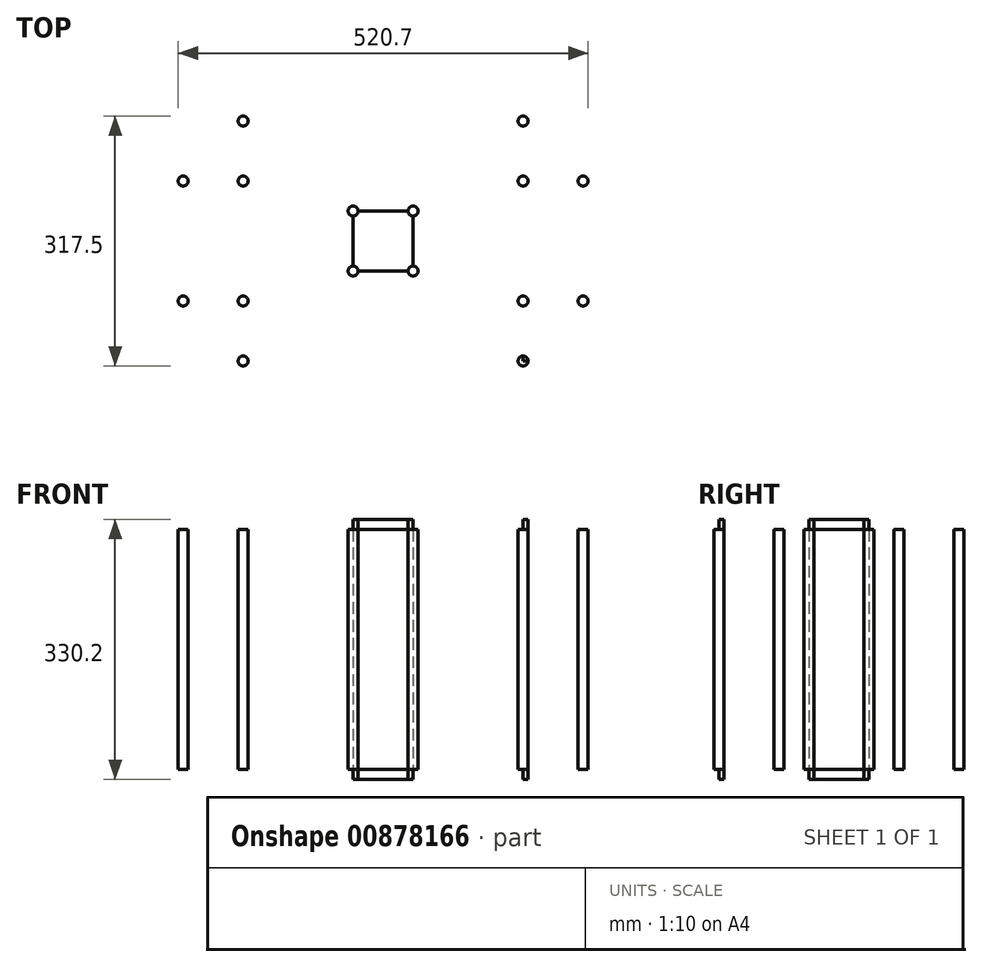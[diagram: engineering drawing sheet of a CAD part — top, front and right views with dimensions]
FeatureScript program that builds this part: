
annotation { "Feature Type Name" : "Feature", "Feature Type Description" : "" }
export const myFeature = defineFeature(function(context is Context, id is Id, definition is map)
    precondition{}
    {
        {
            var Q0;
            Q0=qCreatedBy(makeId("Top.planeOp"),FACE);
            var sketch = newSketch(context, id + "F0", { "sketchPlane" : qUnion([Q0])});
            skLineSegment(sketch, "E0.bottom", {"start": v(254, -152.4) * mm, "end": v(-254, -152.4) * mm});
            skLineSegment(sketch, "E0.top", {"start": v(254, 152.4) * mm, "end": v(-254, 152.4) * mm});
            skLineSegment(sketch, "E0.left", {"start": v(254, -152.4) * mm, "end": v(254, 152.4) * mm});
            skLineSegment(sketch, "E0.right", {"start": v(-254, -152.4) * mm, "end": v(-254, 152.4) * mm});
            skPoint(sketch, "E0.middle", {"position": v(0, 0) * mm});
            skLineSegment(sketch, "E1.bottom", {"start": v(-254, 152.4) * mm, "end": v(-177.8, 152.4) * mm});
            skLineSegment(sketch, "E1.top", {"start": v(-254, 76.2) * mm, "end": v(-177.8, 76.2) * mm});
            skLineSegment(sketch, "E1.left", {"start": v(-254, 152.4) * mm, "end": v(-254, 76.2) * mm});
            skLineSegment(sketch, "E1.right", {"start": v(-177.8, 152.4) * mm, "end": v(-177.8, 76.2) * mm});
            skLineSegment(sketch, "E2.bottom", {"start": v(254, 152.4) * mm, "end": v(177.8, 152.4) * mm});
            skLineSegment(sketch, "E2.top", {"start": v(254, 76.2) * mm, "end": v(177.8, 76.2) * mm});
            skLineSegment(sketch, "E2.left", {"start": v(254, 152.4) * mm, "end": v(254, 76.2) * mm});
            skLineSegment(sketch, "E2.right", {"start": v(177.8, 152.4) * mm, "end": v(177.8, 76.2) * mm});
            skLineSegment(sketch, "E3.bottom", {"start": v(254, -152.4) * mm, "end": v(177.8, -152.4) * mm});
            skLineSegment(sketch, "E3.top", {"start": v(254, -76.2) * mm, "end": v(177.8, -76.2) * mm});
            skLineSegment(sketch, "E3.left", {"start": v(254, -152.4) * mm, "end": v(254, -76.2) * mm});
            skLineSegment(sketch, "E3.right", {"start": v(177.8, -152.4) * mm, "end": v(177.8, -76.2) * mm});
            skLineSegment(sketch, "E4.bottom", {"start": v(-254, -152.4) * mm, "end": v(-177.8, -152.4) * mm});
            skLineSegment(sketch, "E4.top", {"start": v(-254, -76.2) * mm, "end": v(-177.8, -76.2) * mm});
            skLineSegment(sketch, "E4.left", {"start": v(-254, -152.4) * mm, "end": v(-254, -76.2) * mm});
            skLineSegment(sketch, "E4.right", {"start": v(-177.8, -152.4) * mm, "end": v(-177.8, -76.2) * mm});
            skLineSegment(sketch, "E5.bottom", {"start": v(38.1, 38.1) * mm, "end": v(-38.1, 38.1) * mm});
            skLineSegment(sketch, "E5.top", {"start": v(38.1, -38.1) * mm, "end": v(-38.1, -38.1) * mm});
            skLineSegment(sketch, "E5.left", {"start": v(38.1, 38.1) * mm, "end": v(38.1, -38.1) * mm});
            skLineSegment(sketch, "E5.right", {"start": v(-38.1, 38.1) * mm, "end": v(-38.1, -38.1) * mm});
            skCircle(sketch, "E6", {"center": v(-177.8, 76.2) * mm, "radius": 6.35 * mm});
            skCircle(sketch, "E7", {"center": v(-254, 152.4) * mm, "radius": 6.35 * mm});
            skCircle(sketch, "E8", {"center": v(-177.8, 152.4) * mm, "radius": 6.35 * mm});
            skCircle(sketch, "E9", {"center": v(-254, 76.2) * mm, "radius": 6.35 * mm});
            skCircle(sketch, "E10", {"center": v(-254, -152.4) * mm, "radius": 6.35 * mm});
            skCircle(sketch, "E11", {"center": v(-254, -76.2) * mm, "radius": 6.35 * mm});
            skCircle(sketch, "E12", {"center": v(-177.8, -152.4) * mm, "radius": 6.35 * mm});
            skCircle(sketch, "E13", {"center": v(-177.8, -76.2) * mm, "radius": 6.35 * mm});
            skCircle(sketch, "E14", {"center": v(-38.1, 38.1) * mm, "radius": 6.35 * mm});
            skCircle(sketch, "E15", {"center": v(-38.1, -38.1) * mm, "radius": 6.35 * mm});
            skCircle(sketch, "E16", {"center": v(38.1, -38.1) * mm, "radius": 6.35 * mm});
            skCircle(sketch, "E17", {"center": v(38.1, 38.1) * mm, "radius": 6.35 * mm});
            skCircle(sketch, "E18", {"center": v(177.8, -152.4) * mm, "radius": 6.35 * mm});
            skCircle(sketch, "E19", {"center": v(177.8, -76.2) * mm, "radius": 6.35 * mm});
            skCircle(sketch, "E20", {"center": v(254, -152.4) * mm, "radius": 6.35 * mm});
            skCircle(sketch, "E21", {"center": v(254, -76.2) * mm, "radius": 6.35 * mm});
            skCircle(sketch, "E22", {"center": v(177.8, 76.2) * mm, "radius": 6.35 * mm});
            skCircle(sketch, "E23", {"center": v(177.8, 152.4) * mm, "radius": 6.35 * mm});
            skCircle(sketch, "E24", {"center": v(254, 152.4) * mm, "radius": 6.35 * mm});
            skCircle(sketch, "E25", {"center": v(254, 76.2) * mm, "radius": 6.35 * mm});
            skSolve(sketch);
        }
        {
            var Q0;
            {var subQ11=sQuery(id+"F0.wireOp",EDGE,"E0.bottom");var subQ51=sQuery(id+"F0.wireOp",EDGE,"E18");var subQ52=makeQuery(id+"F0.imprint","INTERSECT",VERTEX,{"derivedFrom":[subQ11,subQ51]});Q0=makeQuery(id+"F0.imprint","IMPRINT",FACE,{"disambiguationData":[TD([[makeQuery(id+"F0.imprint","IMPRINT",EDGE,{"disambiguationData":[TD([[subQ52,-1.0]])],"derivedFrom":subQ11}),-1.0]])]});}
            var Q1;
            {var subQ5=sQuery(id+"F0.wireOp",EDGE,"E17");var subQ13=sQuery(id+"F0.wireOp",EDGE,"E5.bottom");var subQ14=makeQuery(id+"F0.imprint","INTERSECT",VERTEX,{"derivedFrom":[subQ13,subQ5]});Q1=makeQuery(id+"F0.imprint","IMPRINT",FACE,{"disambiguationData":[TD([[makeQuery(id+"F0.imprint","IMPRINT",EDGE,{"disambiguationData":[TD([[subQ14,-1.0]])],"derivedFrom":subQ13}),1.0]])]});}
            var Q2;
            {var subQ5=sQuery(id+"F0.wireOp",EDGE,"E24");var subQ13=sQuery(id+"F0.wireOp",EDGE,"E2.bottom");var subQ14=makeQuery(id+"F0.imprint","INTERSECT",VERTEX,{"derivedFrom":[subQ13,subQ5]});Q2=makeQuery(id+"F0.imprint","IMPRINT",FACE,{"disambiguationData":[TD([[makeQuery(id+"F0.imprint","IMPRINT",EDGE,{"disambiguationData":[TD([[subQ14,-1.0]])],"derivedFrom":subQ13}),1.0]])]});}
            var Q3;
            {var subQ5=sQuery(id+"F0.wireOp",EDGE,"E20");var subQ13=sQuery(id+"F0.wireOp",EDGE,"E3.bottom");var subQ14=makeQuery(id+"F0.imprint","INTERSECT",VERTEX,{"derivedFrom":[subQ13,subQ5]});Q3=makeQuery(id+"F0.imprint","IMPRINT",FACE,{"disambiguationData":[TD([[makeQuery(id+"F0.imprint","IMPRINT",EDGE,{"disambiguationData":[TD([[subQ14,-1.0]])],"derivedFrom":subQ13}),-1.0]])]});}
            var Q4;
            {var subQ5=sQuery(id+"F0.wireOp",EDGE,"E10");var subQ10=sQuery(id+"F0.wireOp",EDGE,"E4.bottom");var subQ15=makeQuery(id+"F0.imprint","INTERSECT",VERTEX,{"derivedFrom":[subQ10,subQ5]});Q4=makeQuery(id+"F0.imprint","IMPRINT",FACE,{"disambiguationData":[TD([[makeQuery(id+"F0.imprint","IMPRINT",EDGE,{"disambiguationData":[TD([[subQ15,-1.0]])],"derivedFrom":subQ10}),1.0]])]});}
            var Q5;
            {var subQ5=sQuery(id+"F0.wireOp",EDGE,"E1.bottom");var subQ7=sQuery(id+"F0.wireOp",EDGE,"E7");var subQ15=makeQuery(id+"F0.imprint","INTERSECT",VERTEX,{"derivedFrom":[subQ5,subQ7]});Q5=makeQuery(id+"F0.imprint","IMPRINT",FACE,{"disambiguationData":[TD([[makeQuery(id+"F0.imprint","IMPRINT",EDGE,{"disambiguationData":[TD([[subQ15,-1.0]])],"derivedFrom":subQ5}),-1.0]])]});}
            extrude(context, id + "F1", {"entities" : qUnion([Q0, Q1, Q2, Q3, Q4, Q5]), "depth" : 317.5 * mm, "offsetDistance" : 25.4 * mm});
        }
        {
            var Q0;
            {var subQ11=sQuery(id+"F0.wireOp",EDGE,"E0.bottom");var subQ51=sQuery(id+"F0.wireOp",EDGE,"E18");var subQ52=makeQuery(id+"F0.imprint","INTERSECT",VERTEX,{"derivedFrom":[subQ11,subQ51]});Q0=makeQuery(id+"F0.imprint","IMPRINT",FACE,{"disambiguationData":[TD([[makeQuery(id+"F0.imprint","IMPRINT",EDGE,{"disambiguationData":[TD([[subQ52,-1.0]])],"derivedFrom":subQ11}),-1.0]])]});}
            var Q1;
            {var subQ5=sQuery(id+"F0.wireOp",EDGE,"E1.bottom");var subQ7=sQuery(id+"F0.wireOp",EDGE,"E7");var subQ15=makeQuery(id+"F0.imprint","INTERSECT",VERTEX,{"derivedFrom":[subQ5,subQ7]});Q1=makeQuery(id+"F0.imprint","IMPRINT",FACE,{"disambiguationData":[TD([[makeQuery(id+"F0.imprint","IMPRINT",EDGE,{"disambiguationData":[TD([[subQ15,-1.0]])],"derivedFrom":subQ5}),-1.0]])]});}
            var Q2;
            {var subQ5=sQuery(id+"F0.wireOp",EDGE,"E10");var subQ10=sQuery(id+"F0.wireOp",EDGE,"E4.bottom");var subQ15=makeQuery(id+"F0.imprint","INTERSECT",VERTEX,{"derivedFrom":[subQ10,subQ5]});Q2=makeQuery(id+"F0.imprint","IMPRINT",FACE,{"disambiguationData":[TD([[makeQuery(id+"F0.imprint","IMPRINT",EDGE,{"disambiguationData":[TD([[subQ15,-1.0]])],"derivedFrom":subQ10}),1.0]])]});}
            var Q3;
            {var subQ5=sQuery(id+"F0.wireOp",EDGE,"E20");var subQ13=sQuery(id+"F0.wireOp",EDGE,"E3.bottom");var subQ14=makeQuery(id+"F0.imprint","INTERSECT",VERTEX,{"derivedFrom":[subQ13,subQ5]});Q3=makeQuery(id+"F0.imprint","IMPRINT",FACE,{"disambiguationData":[TD([[makeQuery(id+"F0.imprint","IMPRINT",EDGE,{"disambiguationData":[TD([[subQ14,-1.0]])],"derivedFrom":subQ13}),-1.0]])]});}
            var Q4;
            {var subQ5=sQuery(id+"F0.wireOp",EDGE,"E24");var subQ13=sQuery(id+"F0.wireOp",EDGE,"E2.bottom");var subQ14=makeQuery(id+"F0.imprint","INTERSECT",VERTEX,{"derivedFrom":[subQ13,subQ5]});Q4=makeQuery(id+"F0.imprint","IMPRINT",FACE,{"disambiguationData":[TD([[makeQuery(id+"F0.imprint","IMPRINT",EDGE,{"disambiguationData":[TD([[subQ14,-1.0]])],"derivedFrom":subQ13}),1.0]])]});}
            var Q5;
            {var subQ5=sQuery(id+"F0.wireOp",EDGE,"E17");var subQ13=sQuery(id+"F0.wireOp",EDGE,"E5.bottom");var subQ14=makeQuery(id+"F0.imprint","INTERSECT",VERTEX,{"derivedFrom":[subQ13,subQ5]});Q5=makeQuery(id+"F0.imprint","IMPRINT",FACE,{"disambiguationData":[TD([[makeQuery(id+"F0.imprint","IMPRINT",EDGE,{"disambiguationData":[TD([[subQ14,-1.0]])],"derivedFrom":subQ13}),1.0]])]});}
            extrude(context, id + "F2", {"entities" : qUnion([Q0, Q1, Q2, Q3, Q4, Q5]), "operationType" : NewBodyOperationType.REMOVE, "depth" : 304.8 * mm, "offsetDistance" : 25.4 * mm});
        }
        {
            var Q0;
            {var subQ0=sQuery(id+"F0.wireOp",EDGE,"E1.left");var subQ1=sQuery(id+"F0.wireOp",EDGE,"E1.bottom");var subQ2=makeQuery(id+"F0.imprint","INTERSECT",VERTEX,{"derivedFrom":[subQ1,subQ0]});Q0=makeQuery(id+"F0.imprint","IMPRINT",FACE,{"disambiguationData":[TD([[makeQuery(id+"F0.imprint","IMPRINT",EDGE,{"disambiguationData":[TD([[subQ2,-1.0]])],"derivedFrom":subQ1}),1.0]])]});}
            var Q1;
            {var subQ0=sQuery(id+"F0.wireOp",EDGE,"E2.left");var subQ1=sQuery(id+"F0.wireOp",EDGE,"E2.bottom");var subQ2=makeQuery(id+"F0.imprint","INTERSECT",VERTEX,{"derivedFrom":[subQ1,subQ0]});Q1=makeQuery(id+"F0.imprint","IMPRINT",FACE,{"disambiguationData":[TD([[makeQuery(id+"F0.imprint","IMPRINT",EDGE,{"disambiguationData":[TD([[subQ2,-1.0]])],"derivedFrom":subQ1}),-1.0]])]});}
            var Q2;
            {var subQ0=sQuery(id+"F0.wireOp",EDGE,"E3.left");var subQ1=sQuery(id+"F0.wireOp",EDGE,"E3.bottom");var subQ2=makeQuery(id+"F0.imprint","INTERSECT",VERTEX,{"derivedFrom":[subQ1,subQ0]});Q2=makeQuery(id+"F0.imprint","IMPRINT",FACE,{"disambiguationData":[TD([[makeQuery(id+"F0.imprint","IMPRINT",EDGE,{"disambiguationData":[TD([[subQ2,-1.0]])],"derivedFrom":subQ1}),1.0]])]});}
            var Q3;
            {var subQ0=sQuery(id+"F0.wireOp",EDGE,"E4.left");var subQ1=sQuery(id+"F0.wireOp",EDGE,"E4.bottom");var subQ2=makeQuery(id+"F0.imprint","INTERSECT",VERTEX,{"derivedFrom":[subQ1,subQ0]});Q3=makeQuery(id+"F0.imprint","IMPRINT",FACE,{"disambiguationData":[TD([[makeQuery(id+"F0.imprint","IMPRINT",EDGE,{"disambiguationData":[TD([[subQ2,-1.0]])],"derivedFrom":subQ1}),-1.0]])]});}
            var Q4;
            {var subQ1=sQuery(id+"F0.wireOp",EDGE,"E0.bottom");var subQ3=sQuery(id+"F0.wireOp",EDGE,"E18");var subQ4=makeQuery(id+"F0.imprint","INTERSECT",VERTEX,{"derivedFrom":[subQ1,subQ3]});Q4=makeQuery(id+"F0.imprint","IMPRINT",FACE,{"disambiguationData":[TD([[makeQuery(id+"F0.imprint","IMPRINT",EDGE,{"disambiguationData":[TD([[subQ4,-1.0]])],"derivedFrom":subQ3}),1.0]])]});}
            var Q5;
            {var subQ1=sQuery(id+"F0.wireOp",EDGE,"E0.bottom");var subQ3=sQuery(id+"F0.wireOp",EDGE,"E12");var subQ4=makeQuery(id+"F0.imprint","INTERSECT",VERTEX,{"derivedFrom":[subQ1,subQ3]});Q5=makeQuery(id+"F0.imprint","IMPRINT",FACE,{"disambiguationData":[TD([[makeQuery(id+"F0.imprint","IMPRINT",EDGE,{"disambiguationData":[TD([[subQ4,1.0]])],"derivedFrom":subQ3}),1.0]])]});}
            var Q6;
            {var subQ1=sQuery(id+"F0.wireOp",EDGE,"E0.top");var subQ3=sQuery(id+"F0.wireOp",EDGE,"E23");var subQ4=makeQuery(id+"F0.imprint","INTERSECT",VERTEX,{"derivedFrom":[subQ1,subQ3]});Q6=makeQuery(id+"F0.imprint","IMPRINT",FACE,{"disambiguationData":[TD([[makeQuery(id+"F0.imprint","IMPRINT",EDGE,{"disambiguationData":[TD([[subQ4,1.0]])],"derivedFrom":subQ3}),1.0]])]});}
            var Q7;
            {var subQ1=sQuery(id+"F0.wireOp",EDGE,"E0.top");var subQ3=sQuery(id+"F0.wireOp",EDGE,"E8");var subQ4=makeQuery(id+"F0.imprint","INTERSECT",VERTEX,{"derivedFrom":[subQ1,subQ3]});Q7=makeQuery(id+"F0.imprint","IMPRINT",FACE,{"disambiguationData":[TD([[makeQuery(id+"F0.imprint","IMPRINT",EDGE,{"disambiguationData":[TD([[subQ4,-1.0]])],"derivedFrom":subQ3}),1.0]])]});}
            var Q8;
            {var subQ1=sQuery(id+"F0.wireOp",EDGE,"E0.left");var subQ3=sQuery(id+"F0.wireOp",EDGE,"E21");var subQ4=makeQuery(id+"F0.imprint","INTERSECT",VERTEX,{"derivedFrom":[subQ1,subQ3]});Q8=makeQuery(id+"F0.imprint","IMPRINT",FACE,{"disambiguationData":[TD([[makeQuery(id+"F0.imprint","IMPRINT",EDGE,{"disambiguationData":[TD([[subQ4,1.0]])],"derivedFrom":subQ3}),1.0]])]});}
            var Q9;
            {var subQ1=sQuery(id+"F0.wireOp",EDGE,"E0.left");var subQ3=sQuery(id+"F0.wireOp",EDGE,"E25");var subQ4=makeQuery(id+"F0.imprint","INTERSECT",VERTEX,{"derivedFrom":[subQ1,subQ3]});Q9=makeQuery(id+"F0.imprint","IMPRINT",FACE,{"disambiguationData":[TD([[makeQuery(id+"F0.imprint","IMPRINT",EDGE,{"disambiguationData":[TD([[subQ4,-1.0]])],"derivedFrom":subQ3}),1.0]])]});}
            var Q10;
            {var subQ1=sQuery(id+"F0.wireOp",EDGE,"E0.right");var subQ3=sQuery(id+"F0.wireOp",EDGE,"E11");var subQ4=makeQuery(id+"F0.imprint","INTERSECT",VERTEX,{"derivedFrom":[subQ1,subQ3]});Q10=makeQuery(id+"F0.imprint","IMPRINT",FACE,{"disambiguationData":[TD([[makeQuery(id+"F0.imprint","IMPRINT",EDGE,{"disambiguationData":[TD([[subQ4,-1.0]])],"derivedFrom":subQ3}),1.0]])]});}
            var Q11;
            {var subQ1=sQuery(id+"F0.wireOp",EDGE,"E0.right");var subQ3=sQuery(id+"F0.wireOp",EDGE,"E9");var subQ4=makeQuery(id+"F0.imprint","INTERSECT",VERTEX,{"derivedFrom":[subQ1,subQ3]});Q11=makeQuery(id+"F0.imprint","IMPRINT",FACE,{"disambiguationData":[TD([[makeQuery(id+"F0.imprint","IMPRINT",EDGE,{"disambiguationData":[TD([[subQ4,1.0]])],"derivedFrom":subQ3}),1.0]])]});}
            var Q12;
            {var subQ0=sQuery(id+"F0.wireOp",EDGE,"E1.left");var subQ1=sQuery(id+"F0.wireOp",EDGE,"E1.bottom");var subQ2=makeQuery(id+"F0.imprint","INTERSECT",VERTEX,{"derivedFrom":[subQ1,subQ0]});Q12=makeQuery(id+"F0.imprint","IMPRINT",FACE,{"disambiguationData":[TD([[makeQuery(id+"F0.imprint","IMPRINT",EDGE,{"disambiguationData":[TD([[subQ2,-1.0]])],"derivedFrom":subQ1}),-1.0]])]});}
            var Q13;
            {var subQ0=sQuery(id+"F0.wireOp",EDGE,"E2.left");var subQ1=sQuery(id+"F0.wireOp",EDGE,"E2.bottom");var subQ2=makeQuery(id+"F0.imprint","INTERSECT",VERTEX,{"derivedFrom":[subQ1,subQ0]});Q13=makeQuery(id+"F0.imprint","IMPRINT",FACE,{"disambiguationData":[TD([[makeQuery(id+"F0.imprint","IMPRINT",EDGE,{"disambiguationData":[TD([[subQ2,-1.0]])],"derivedFrom":subQ1}),1.0]])]});}
            var Q14;
            {var subQ0=sQuery(id+"F0.wireOp",EDGE,"E3.left");var subQ1=sQuery(id+"F0.wireOp",EDGE,"E3.bottom");var subQ2=makeQuery(id+"F0.imprint","INTERSECT",VERTEX,{"derivedFrom":[subQ1,subQ0]});Q14=makeQuery(id+"F0.imprint","IMPRINT",FACE,{"disambiguationData":[TD([[makeQuery(id+"F0.imprint","IMPRINT",EDGE,{"disambiguationData":[TD([[subQ2,-1.0]])],"derivedFrom":subQ1}),-1.0]])]});}
            var Q15;
            {var subQ0=sQuery(id+"F0.wireOp",EDGE,"E4.left");var subQ1=sQuery(id+"F0.wireOp",EDGE,"E4.bottom");var subQ2=makeQuery(id+"F0.imprint","INTERSECT",VERTEX,{"derivedFrom":[subQ1,subQ0]});Q15=makeQuery(id+"F0.imprint","IMPRINT",FACE,{"disambiguationData":[TD([[makeQuery(id+"F0.imprint","IMPRINT",EDGE,{"disambiguationData":[TD([[subQ2,-1.0]])],"derivedFrom":subQ1}),1.0]])]});}
            var Q16;
            {var subQ1=sQuery(id+"F0.wireOp",EDGE,"E0.bottom");var subQ3=sQuery(id+"F0.wireOp",EDGE,"E18");var subQ4=makeQuery(id+"F0.imprint","INTERSECT",VERTEX,{"derivedFrom":[subQ1,subQ3]});Q16=makeQuery(id+"F0.imprint","IMPRINT",FACE,{"disambiguationData":[TD([[makeQuery(id+"F0.imprint","IMPRINT",EDGE,{"disambiguationData":[TD([[subQ4,1.0]])],"derivedFrom":subQ3}),1.0]])]});}
            var Q17;
            {var subQ1=sQuery(id+"F0.wireOp",EDGE,"E0.bottom");var subQ3=sQuery(id+"F0.wireOp",EDGE,"E12");var subQ4=makeQuery(id+"F0.imprint","INTERSECT",VERTEX,{"derivedFrom":[subQ1,subQ3]});Q17=makeQuery(id+"F0.imprint","IMPRINT",FACE,{"disambiguationData":[TD([[makeQuery(id+"F0.imprint","IMPRINT",EDGE,{"disambiguationData":[TD([[subQ4,-1.0]])],"derivedFrom":subQ3}),1.0]])]});}
            var Q18;
            {var subQ1=sQuery(id+"F0.wireOp",EDGE,"E0.top");var subQ3=sQuery(id+"F0.wireOp",EDGE,"E23");var subQ4=makeQuery(id+"F0.imprint","INTERSECT",VERTEX,{"derivedFrom":[subQ1,subQ3]});Q18=makeQuery(id+"F0.imprint","IMPRINT",FACE,{"disambiguationData":[TD([[makeQuery(id+"F0.imprint","IMPRINT",EDGE,{"disambiguationData":[TD([[subQ4,-1.0]])],"derivedFrom":subQ3}),1.0]])]});}
            var Q19;
            {var subQ1=sQuery(id+"F0.wireOp",EDGE,"E0.top");var subQ3=sQuery(id+"F0.wireOp",EDGE,"E8");var subQ4=makeQuery(id+"F0.imprint","INTERSECT",VERTEX,{"derivedFrom":[subQ1,subQ3]});Q19=makeQuery(id+"F0.imprint","IMPRINT",FACE,{"disambiguationData":[TD([[makeQuery(id+"F0.imprint","IMPRINT",EDGE,{"disambiguationData":[TD([[subQ4,1.0]])],"derivedFrom":subQ3}),1.0]])]});}
            var Q20;
            {var subQ1=sQuery(id+"F0.wireOp",EDGE,"E0.left");var subQ3=sQuery(id+"F0.wireOp",EDGE,"E21");var subQ4=makeQuery(id+"F0.imprint","INTERSECT",VERTEX,{"derivedFrom":[subQ1,subQ3]});Q20=makeQuery(id+"F0.imprint","IMPRINT",FACE,{"disambiguationData":[TD([[makeQuery(id+"F0.imprint","IMPRINT",EDGE,{"disambiguationData":[TD([[subQ4,-1.0]])],"derivedFrom":subQ3}),1.0]])]});}
            var Q21;
            {var subQ1=sQuery(id+"F0.wireOp",EDGE,"E0.left");var subQ3=sQuery(id+"F0.wireOp",EDGE,"E25");var subQ4=makeQuery(id+"F0.imprint","INTERSECT",VERTEX,{"derivedFrom":[subQ1,subQ3]});Q21=makeQuery(id+"F0.imprint","IMPRINT",FACE,{"disambiguationData":[TD([[makeQuery(id+"F0.imprint","IMPRINT",EDGE,{"disambiguationData":[TD([[subQ4,1.0]])],"derivedFrom":subQ3}),1.0]])]});}
            var Q22;
            {var subQ1=sQuery(id+"F0.wireOp",EDGE,"E0.right");var subQ3=sQuery(id+"F0.wireOp",EDGE,"E11");var subQ4=makeQuery(id+"F0.imprint","INTERSECT",VERTEX,{"derivedFrom":[subQ1,subQ3]});Q22=makeQuery(id+"F0.imprint","IMPRINT",FACE,{"disambiguationData":[TD([[makeQuery(id+"F0.imprint","IMPRINT",EDGE,{"disambiguationData":[TD([[subQ4,1.0]])],"derivedFrom":subQ3}),1.0]])]});}
            var Q23;
            {var subQ1=sQuery(id+"F0.wireOp",EDGE,"E0.right");var subQ3=sQuery(id+"F0.wireOp",EDGE,"E9");var subQ4=makeQuery(id+"F0.imprint","INTERSECT",VERTEX,{"derivedFrom":[subQ1,subQ3]});Q23=makeQuery(id+"F0.imprint","IMPRINT",FACE,{"disambiguationData":[TD([[makeQuery(id+"F0.imprint","IMPRINT",EDGE,{"disambiguationData":[TD([[subQ4,-1.0]])],"derivedFrom":subQ3}),1.0]])]});}
            var Q24;
            {var subQ1=sQuery(id+"F0.wireOp",EDGE,"E1.bottom");var subQ3=sQuery(id+"F0.wireOp",EDGE,"E8");var subQ4=makeQuery(id+"F0.imprint","INTERSECT",VERTEX,{"derivedFrom":[subQ1,subQ3]});Q24=makeQuery(id+"F0.imprint","IMPRINT",FACE,{"disambiguationData":[TD([[makeQuery(id+"F0.imprint","IMPRINT",EDGE,{"disambiguationData":[TD([[subQ4,-1.0]])],"derivedFrom":subQ3}),1.0]])]});}
            var Q25;
            {var subQ0=sQuery(id+"F0.wireOp",EDGE,"E1.left");var subQ3=sQuery(id+"F0.wireOp",EDGE,"E9");var subQ5=makeQuery(id+"F0.imprint","INTERSECT",VERTEX,{"derivedFrom":[subQ0,subQ3]});Q25=makeQuery(id+"F0.imprint","IMPRINT",FACE,{"disambiguationData":[TD([[makeQuery(id+"F0.imprint","IMPRINT",EDGE,{"disambiguationData":[TD([[subQ5,1.0]])],"derivedFrom":subQ3}),1.0]])]});}
            var Q26;
            {var subQ1=sQuery(id+"F0.wireOp",EDGE,"E2.bottom");var subQ3=sQuery(id+"F0.wireOp",EDGE,"E23");var subQ4=makeQuery(id+"F0.imprint","INTERSECT",VERTEX,{"derivedFrom":[subQ1,subQ3]});Q26=makeQuery(id+"F0.imprint","IMPRINT",FACE,{"disambiguationData":[TD([[makeQuery(id+"F0.imprint","IMPRINT",EDGE,{"disambiguationData":[TD([[subQ4,1.0]])],"derivedFrom":subQ3}),1.0]])]});}
            var Q27;
            {var subQ0=sQuery(id+"F0.wireOp",EDGE,"E2.left");var subQ3=sQuery(id+"F0.wireOp",EDGE,"E25");var subQ5=makeQuery(id+"F0.imprint","INTERSECT",VERTEX,{"derivedFrom":[subQ0,subQ3]});Q27=makeQuery(id+"F0.imprint","IMPRINT",FACE,{"disambiguationData":[TD([[makeQuery(id+"F0.imprint","IMPRINT",EDGE,{"disambiguationData":[TD([[subQ5,-1.0]])],"derivedFrom":subQ3}),1.0]])]});}
            var Q28;
            {var subQ1=sQuery(id+"F0.wireOp",EDGE,"E3.bottom");var subQ3=sQuery(id+"F0.wireOp",EDGE,"E18");var subQ4=makeQuery(id+"F0.imprint","INTERSECT",VERTEX,{"derivedFrom":[subQ1,subQ3]});Q28=makeQuery(id+"F0.imprint","IMPRINT",FACE,{"disambiguationData":[TD([[makeQuery(id+"F0.imprint","IMPRINT",EDGE,{"disambiguationData":[TD([[subQ4,-1.0]])],"derivedFrom":subQ3}),1.0]])]});}
            var Q29;
            {var subQ0=sQuery(id+"F0.wireOp",EDGE,"E3.left");var subQ3=sQuery(id+"F0.wireOp",EDGE,"E21");var subQ5=makeQuery(id+"F0.imprint","INTERSECT",VERTEX,{"derivedFrom":[subQ0,subQ3]});Q29=makeQuery(id+"F0.imprint","IMPRINT",FACE,{"disambiguationData":[TD([[makeQuery(id+"F0.imprint","IMPRINT",EDGE,{"disambiguationData":[TD([[subQ5,1.0]])],"derivedFrom":subQ3}),1.0]])]});}
            var Q30;
            {var subQ1=sQuery(id+"F0.wireOp",EDGE,"E4.bottom");var subQ3=sQuery(id+"F0.wireOp",EDGE,"E12");var subQ4=makeQuery(id+"F0.imprint","INTERSECT",VERTEX,{"derivedFrom":[subQ1,subQ3]});Q30=makeQuery(id+"F0.imprint","IMPRINT",FACE,{"disambiguationData":[TD([[makeQuery(id+"F0.imprint","IMPRINT",EDGE,{"disambiguationData":[TD([[subQ4,1.0]])],"derivedFrom":subQ3}),1.0]])]});}
            var Q31;
            {var subQ0=sQuery(id+"F0.wireOp",EDGE,"E4.left");var subQ3=sQuery(id+"F0.wireOp",EDGE,"E11");var subQ5=makeQuery(id+"F0.imprint","INTERSECT",VERTEX,{"derivedFrom":[subQ0,subQ3]});Q31=makeQuery(id+"F0.imprint","IMPRINT",FACE,{"disambiguationData":[TD([[makeQuery(id+"F0.imprint","IMPRINT",EDGE,{"disambiguationData":[TD([[subQ5,-1.0]])],"derivedFrom":subQ3}),1.0]])]});}
            var Q32;
            {var subQ5=sQuery(id+"F0.wireOp",EDGE,"E1.bottom");var subQ7=sQuery(id+"F0.wireOp",EDGE,"E7");var subQ15=makeQuery(id+"F0.imprint","INTERSECT",VERTEX,{"derivedFrom":[subQ5,subQ7]});Q32=makeQuery(id+"F0.imprint","IMPRINT",FACE,{"disambiguationData":[TD([[makeQuery(id+"F0.imprint","IMPRINT",EDGE,{"disambiguationData":[TD([[subQ15,-1.0]])],"derivedFrom":subQ5}),-1.0]])]});}
            var Q33;
            {var subQ5=sQuery(id+"F0.wireOp",EDGE,"E24");var subQ13=sQuery(id+"F0.wireOp",EDGE,"E2.bottom");var subQ14=makeQuery(id+"F0.imprint","INTERSECT",VERTEX,{"derivedFrom":[subQ13,subQ5]});Q33=makeQuery(id+"F0.imprint","IMPRINT",FACE,{"disambiguationData":[TD([[makeQuery(id+"F0.imprint","IMPRINT",EDGE,{"disambiguationData":[TD([[subQ14,-1.0]])],"derivedFrom":subQ13}),1.0]])]});}
            var Q34;
            {var subQ5=sQuery(id+"F0.wireOp",EDGE,"E20");var subQ13=sQuery(id+"F0.wireOp",EDGE,"E3.bottom");var subQ14=makeQuery(id+"F0.imprint","INTERSECT",VERTEX,{"derivedFrom":[subQ13,subQ5]});Q34=makeQuery(id+"F0.imprint","IMPRINT",FACE,{"disambiguationData":[TD([[makeQuery(id+"F0.imprint","IMPRINT",EDGE,{"disambiguationData":[TD([[subQ14,-1.0]])],"derivedFrom":subQ13}),-1.0]])]});}
            var Q35;
            {var subQ5=sQuery(id+"F0.wireOp",EDGE,"E10");var subQ10=sQuery(id+"F0.wireOp",EDGE,"E4.bottom");var subQ15=makeQuery(id+"F0.imprint","INTERSECT",VERTEX,{"derivedFrom":[subQ10,subQ5]});Q35=makeQuery(id+"F0.imprint","IMPRINT",FACE,{"disambiguationData":[TD([[makeQuery(id+"F0.imprint","IMPRINT",EDGE,{"disambiguationData":[TD([[subQ15,-1.0]])],"derivedFrom":subQ10}),1.0]])]});}
            var Q36;
            {var subQ0=sQuery(id+"F0.wireOp",EDGE,"E3.right");var subQ1=sQuery(id+"F0.wireOp",EDGE,"E3.top");var subQ2=makeQuery(id+"F0.imprint","INTERSECT",VERTEX,{"derivedFrom":[subQ1,subQ0]});Q36=makeQuery(id+"F0.imprint","IMPRINT",FACE,{"disambiguationData":[TD([[makeQuery(id+"F0.imprint","IMPRINT",EDGE,{"disambiguationData":[TD([[subQ2,1.0]])],"derivedFrom":subQ1}),-1.0]])]});}
            var Q37;
            {var subQ0=sQuery(id+"F0.wireOp",EDGE,"E3.right");var subQ1=sQuery(id+"F0.wireOp",EDGE,"E3.top");var subQ2=makeQuery(id+"F0.imprint","INTERSECT",VERTEX,{"derivedFrom":[subQ1,subQ0]});Q37=makeQuery(id+"F0.imprint","IMPRINT",FACE,{"disambiguationData":[TD([[makeQuery(id+"F0.imprint","IMPRINT",EDGE,{"disambiguationData":[TD([[subQ2,1.0]])],"derivedFrom":subQ1}),1.0]])]});}
            var Q38;
            {var subQ0=sQuery(id+"F0.wireOp",EDGE,"E5.right");var subQ1=sQuery(id+"F0.wireOp",EDGE,"E5.top");var subQ2=makeQuery(id+"F0.imprint","INTERSECT",VERTEX,{"derivedFrom":[subQ1,subQ0]});Q38=makeQuery(id+"F0.imprint","IMPRINT",FACE,{"disambiguationData":[TD([[makeQuery(id+"F0.imprint","IMPRINT",EDGE,{"disambiguationData":[TD([[subQ2,1.0]])],"derivedFrom":subQ1}),1.0]])]});}
            var Q39;
            {var subQ0=sQuery(id+"F0.wireOp",EDGE,"E5.right");var subQ1=sQuery(id+"F0.wireOp",EDGE,"E5.top");var subQ2=makeQuery(id+"F0.imprint","INTERSECT",VERTEX,{"derivedFrom":[subQ1,subQ0]});Q39=makeQuery(id+"F0.imprint","IMPRINT",FACE,{"disambiguationData":[TD([[makeQuery(id+"F0.imprint","IMPRINT",EDGE,{"disambiguationData":[TD([[subQ2,1.0]])],"derivedFrom":subQ1}),-1.0]])]});}
            var Q40;
            {var subQ0=sQuery(id+"F0.wireOp",EDGE,"E5.right");var subQ1=sQuery(id+"F0.wireOp",EDGE,"E5.bottom");var subQ2=makeQuery(id+"F0.imprint","INTERSECT",VERTEX,{"derivedFrom":[subQ1,subQ0]});Q40=makeQuery(id+"F0.imprint","IMPRINT",FACE,{"disambiguationData":[TD([[makeQuery(id+"F0.imprint","IMPRINT",EDGE,{"disambiguationData":[TD([[subQ2,1.0]])],"derivedFrom":subQ1}),-1.0]])]});}
            var Q41;
            {var subQ0=sQuery(id+"F0.wireOp",EDGE,"E5.right");var subQ1=sQuery(id+"F0.wireOp",EDGE,"E5.bottom");var subQ2=makeQuery(id+"F0.imprint","INTERSECT",VERTEX,{"derivedFrom":[subQ1,subQ0]});Q41=makeQuery(id+"F0.imprint","IMPRINT",FACE,{"disambiguationData":[TD([[makeQuery(id+"F0.imprint","IMPRINT",EDGE,{"disambiguationData":[TD([[subQ2,1.0]])],"derivedFrom":subQ1}),1.0]])]});}
            var Q42;
            {var subQ0=sQuery(id+"F0.wireOp",EDGE,"E5.left");var subQ1=sQuery(id+"F0.wireOp",EDGE,"E5.bottom");var subQ2=makeQuery(id+"F0.imprint","INTERSECT",VERTEX,{"derivedFrom":[subQ1,subQ0]});Q42=makeQuery(id+"F0.imprint","IMPRINT",FACE,{"disambiguationData":[TD([[makeQuery(id+"F0.imprint","IMPRINT",EDGE,{"disambiguationData":[TD([[subQ2,-1.0]])],"derivedFrom":subQ1}),-1.0]])]});}
            var Q43;
            {var subQ0=sQuery(id+"F0.wireOp",EDGE,"E5.left");var subQ1=sQuery(id+"F0.wireOp",EDGE,"E5.bottom");var subQ2=makeQuery(id+"F0.imprint","INTERSECT",VERTEX,{"derivedFrom":[subQ1,subQ0]});Q43=makeQuery(id+"F0.imprint","IMPRINT",FACE,{"disambiguationData":[TD([[makeQuery(id+"F0.imprint","IMPRINT",EDGE,{"disambiguationData":[TD([[subQ2,-1.0]])],"derivedFrom":subQ1}),1.0]])]});}
            var Q44;
            {var subQ0=sQuery(id+"F0.wireOp",EDGE,"E2.right");var subQ1=sQuery(id+"F0.wireOp",EDGE,"E2.top");var subQ2=makeQuery(id+"F0.imprint","INTERSECT",VERTEX,{"derivedFrom":[subQ1,subQ0]});Q44=makeQuery(id+"F0.imprint","IMPRINT",FACE,{"disambiguationData":[TD([[makeQuery(id+"F0.imprint","IMPRINT",EDGE,{"disambiguationData":[TD([[subQ2,1.0]])],"derivedFrom":subQ1}),-1.0]])]});}
            var Q45;
            {var subQ0=sQuery(id+"F0.wireOp",EDGE,"E2.right");var subQ1=sQuery(id+"F0.wireOp",EDGE,"E2.top");var subQ2=makeQuery(id+"F0.imprint","INTERSECT",VERTEX,{"derivedFrom":[subQ1,subQ0]});Q45=makeQuery(id+"F0.imprint","IMPRINT",FACE,{"disambiguationData":[TD([[makeQuery(id+"F0.imprint","IMPRINT",EDGE,{"disambiguationData":[TD([[subQ2,1.0]])],"derivedFrom":subQ1}),1.0]])]});}
            var Q46;
            {var subQ0=sQuery(id+"F0.wireOp",EDGE,"E1.right");var subQ1=sQuery(id+"F0.wireOp",EDGE,"E1.top");var subQ2=makeQuery(id+"F0.imprint","INTERSECT",VERTEX,{"derivedFrom":[subQ1,subQ0]});Q46=makeQuery(id+"F0.imprint","IMPRINT",FACE,{"disambiguationData":[TD([[makeQuery(id+"F0.imprint","IMPRINT",EDGE,{"disambiguationData":[TD([[subQ2,1.0]])],"derivedFrom":subQ1}),1.0]])]});}
            var Q47;
            {var subQ0=sQuery(id+"F0.wireOp",EDGE,"E1.right");var subQ1=sQuery(id+"F0.wireOp",EDGE,"E1.top");var subQ2=makeQuery(id+"F0.imprint","INTERSECT",VERTEX,{"derivedFrom":[subQ1,subQ0]});Q47=makeQuery(id+"F0.imprint","IMPRINT",FACE,{"disambiguationData":[TD([[makeQuery(id+"F0.imprint","IMPRINT",EDGE,{"disambiguationData":[TD([[subQ2,1.0]])],"derivedFrom":subQ1}),-1.0]])]});}
            var Q48;
            {var subQ0=sQuery(id+"F0.wireOp",EDGE,"E4.right");var subQ1=sQuery(id+"F0.wireOp",EDGE,"E4.top");var subQ2=makeQuery(id+"F0.imprint","INTERSECT",VERTEX,{"derivedFrom":[subQ1,subQ0]});Q48=makeQuery(id+"F0.imprint","IMPRINT",FACE,{"disambiguationData":[TD([[makeQuery(id+"F0.imprint","IMPRINT",EDGE,{"disambiguationData":[TD([[subQ2,1.0]])],"derivedFrom":subQ1}),1.0]])]});}
            var Q49;
            {var subQ0=sQuery(id+"F0.wireOp",EDGE,"E4.right");var subQ1=sQuery(id+"F0.wireOp",EDGE,"E4.top");var subQ2=makeQuery(id+"F0.imprint","INTERSECT",VERTEX,{"derivedFrom":[subQ1,subQ0]});Q49=makeQuery(id+"F0.imprint","IMPRINT",FACE,{"disambiguationData":[TD([[makeQuery(id+"F0.imprint","IMPRINT",EDGE,{"disambiguationData":[TD([[subQ2,1.0]])],"derivedFrom":subQ1}),-1.0]])]});}
            var Q50;
            {var subQ0=sQuery(id+"F0.wireOp",EDGE,"E5.left");var subQ1=sQuery(id+"F0.wireOp",EDGE,"E5.top");var subQ2=makeQuery(id+"F0.imprint","INTERSECT",VERTEX,{"derivedFrom":[subQ1,subQ0]});Q50=makeQuery(id+"F0.imprint","IMPRINT",FACE,{"disambiguationData":[TD([[makeQuery(id+"F0.imprint","IMPRINT",EDGE,{"disambiguationData":[TD([[subQ2,-1.0]])],"derivedFrom":subQ1}),1.0]])]});}
            var Q51;
            {var subQ0=sQuery(id+"F0.wireOp",EDGE,"E5.left");var subQ1=sQuery(id+"F0.wireOp",EDGE,"E5.top");var subQ2=makeQuery(id+"F0.imprint","INTERSECT",VERTEX,{"derivedFrom":[subQ1,subQ0]});Q51=makeQuery(id+"F0.imprint","IMPRINT",FACE,{"disambiguationData":[TD([[makeQuery(id+"F0.imprint","IMPRINT",EDGE,{"disambiguationData":[TD([[subQ2,-1.0]])],"derivedFrom":subQ1}),-1.0]])]});}
            var Q52;
            {var subQ5=sQuery(id+"F0.wireOp",EDGE,"E17");var subQ13=sQuery(id+"F0.wireOp",EDGE,"E5.bottom");var subQ14=makeQuery(id+"F0.imprint","INTERSECT",VERTEX,{"derivedFrom":[subQ13,subQ5]});Q52=makeQuery(id+"F0.imprint","IMPRINT",FACE,{"disambiguationData":[TD([[makeQuery(id+"F0.imprint","IMPRINT",EDGE,{"disambiguationData":[TD([[subQ14,-1.0]])],"derivedFrom":subQ13}),1.0]])]});}
            extrude(context, id + "F3", {"entities" : qUnion([Q0, Q1, Q2, Q3, Q4, Q5, Q6, Q7, Q8, Q9, Q10, Q11, Q12, Q13, Q14, Q15, Q16, Q17, Q18, Q19, Q20, Q21, Q22, Q23, Q24, Q25, Q26, Q27, Q28, Q29, Q30, Q31, Q32, Q33, Q34, Q35, Q36, Q37, Q38, Q39, Q40, Q41, Q42, Q43, Q44, Q45, Q46, Q47, Q48, Q49, Q50, Q51, Q52]), "depth" : 304.8 * mm, "offsetDistance" : 25.4 * mm});
        }
        {
            var Q0;
            {var subQ5=sQuery(id+"F0.wireOp",EDGE,"E1.bottom");var subQ7=sQuery(id+"F0.wireOp",EDGE,"E7");var subQ15=makeQuery(id+"F0.imprint","INTERSECT",VERTEX,{"derivedFrom":[subQ5,subQ7]});Q0=makeQuery(id+"F0.imprint","IMPRINT",FACE,{"disambiguationData":[TD([[makeQuery(id+"F0.imprint","IMPRINT",EDGE,{"disambiguationData":[TD([[subQ15,-1.0]])],"derivedFrom":subQ5}),-1.0]])]});}
            var Q1;
            {var subQ5=sQuery(id+"F0.wireOp",EDGE,"E10");var subQ10=sQuery(id+"F0.wireOp",EDGE,"E4.bottom");var subQ15=makeQuery(id+"F0.imprint","INTERSECT",VERTEX,{"derivedFrom":[subQ10,subQ5]});Q1=makeQuery(id+"F0.imprint","IMPRINT",FACE,{"disambiguationData":[TD([[makeQuery(id+"F0.imprint","IMPRINT",EDGE,{"disambiguationData":[TD([[subQ15,-1.0]])],"derivedFrom":subQ10}),1.0]])]});}
            var Q2;
            {var subQ5=sQuery(id+"F0.wireOp",EDGE,"E17");var subQ13=sQuery(id+"F0.wireOp",EDGE,"E5.bottom");var subQ14=makeQuery(id+"F0.imprint","INTERSECT",VERTEX,{"derivedFrom":[subQ13,subQ5]});Q2=makeQuery(id+"F0.imprint","IMPRINT",FACE,{"disambiguationData":[TD([[makeQuery(id+"F0.imprint","IMPRINT",EDGE,{"disambiguationData":[TD([[subQ14,-1.0]])],"derivedFrom":subQ13}),1.0]])]});}
            var Q3;
            {var subQ5=sQuery(id+"F0.wireOp",EDGE,"E24");var subQ13=sQuery(id+"F0.wireOp",EDGE,"E2.bottom");var subQ14=makeQuery(id+"F0.imprint","INTERSECT",VERTEX,{"derivedFrom":[subQ13,subQ5]});Q3=makeQuery(id+"F0.imprint","IMPRINT",FACE,{"disambiguationData":[TD([[makeQuery(id+"F0.imprint","IMPRINT",EDGE,{"disambiguationData":[TD([[subQ14,-1.0]])],"derivedFrom":subQ13}),1.0]])]});}
            var Q4;
            {var subQ5=sQuery(id+"F0.wireOp",EDGE,"E20");var subQ13=sQuery(id+"F0.wireOp",EDGE,"E3.bottom");var subQ14=makeQuery(id+"F0.imprint","INTERSECT",VERTEX,{"derivedFrom":[subQ13,subQ5]});Q4=makeQuery(id+"F0.imprint","IMPRINT",FACE,{"disambiguationData":[TD([[makeQuery(id+"F0.imprint","IMPRINT",EDGE,{"disambiguationData":[TD([[subQ14,-1.0]])],"derivedFrom":subQ13}),-1.0]])]});}
            var Q5;
            {var subQ11=sQuery(id+"F0.wireOp",EDGE,"E0.bottom");var subQ51=sQuery(id+"F0.wireOp",EDGE,"E18");var subQ52=makeQuery(id+"F0.imprint","INTERSECT",VERTEX,{"derivedFrom":[subQ11,subQ51]});Q5=makeQuery(id+"F0.imprint","IMPRINT",FACE,{"disambiguationData":[TD([[makeQuery(id+"F0.imprint","IMPRINT",EDGE,{"disambiguationData":[TD([[subQ52,-1.0]])],"derivedFrom":subQ11}),-1.0]])]});}
            extrude(context, id + "F4", {"entities" : qUnion([Q0, Q1, Q2, Q3, Q4, Q5]), "oppositeDirection" : true, "depth" : 12.7 * mm, "offsetDistance" : 25.4 * mm});
        }
    });
